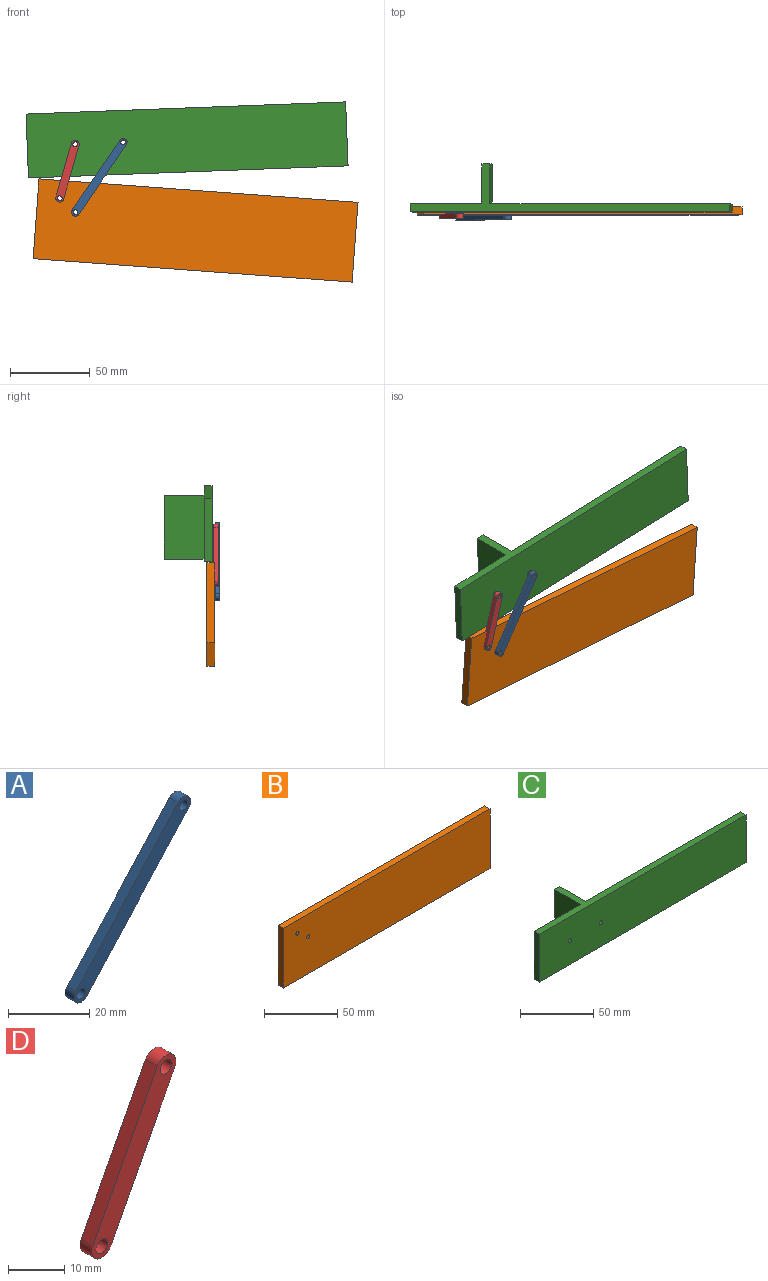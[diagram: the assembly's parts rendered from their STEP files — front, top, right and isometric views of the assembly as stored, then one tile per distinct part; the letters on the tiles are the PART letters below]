
ASSEMBLY  parts=4 mates=5
PART A: 8 faces, bbox 40.6x3x44 mm
  f0: plane 39.02x35.58mm, normal (-0.74,0,0.67), area 158.4mm2, adj f1,f3,f6,f7
  f1: cylinder r=2.5mm len=4.35mm, axis (0,1,0), area 23.6mm2, adj f0,f2,f6,f7
  f2: plane 39.02x35.58mm, normal (0.74,0,-0.67), area 158.4mm2, adj f1,f3,f6,f7
  f3: cylinder r=2.5mm len=4.35mm, axis (0,1,0), area 23.6mm2, adj f0,f2,f6,f7
  f4: cylinder r=1.5mm len=3mm, axis (0,1,0), area 28.3mm2, adj f6,f7
  f5: cylinder r=1.5mm len=3mm, axis (0,1,0), area 28.3mm2, adj f6,f7
  f6: plane 44.02x40.58mm, normal (0,-1,0), area 269.5mm2, adj f0,f1,f2,f3,f4,f5
  f7: plane 44.02x40.58mm, normal (0,1,0), area 269.5mm2, adj f0,f1,f2,f3,f4,f5
PART B: 8 faces, bbox 200x5x50 mm
  f0: plane 200x5mm, normal (0,0,1), area 1000mm2, adj f1,f3,f4,f5
  f1: plane 50x5mm, normal (-1,0,0), area 250mm2, adj f0,f2,f4,f5
  f2: plane 200x5mm, normal (0,0,-1), area 1000mm2, adj f1,f3,f4,f5
  f3: plane 50x5mm, normal (1,0,0), area 250mm2, adj f0,f2,f4,f5
  f4: plane 200x50mm, normal (0,-1,0), area 9985.9mm2, adj f0,f1,f2,f3,f6,f7
  f5: plane 200x50mm, normal (0,1,0), area 9985.9mm2, adj f0,f1,f2,f3,f6,f7
  f6: cylinder r=1.5mm len=5mm, axis (0,1,0), area 47.1mm2, adj f4,f5
  f7: cylinder r=1.5mm len=5mm, axis (0,1,0), area 47.1mm2, adj f4,f5
PART C: 12 faces, bbox 200x30x40 mm
  f0: plane 150x40mm, normal (0,1,0), area 5992.9mm2, adj f1,f3,f4,f8,f11
  f1: plane 200x30mm, normal (0,0,1), area 1125mm2, adj f0,f2,f4,f5,f6,f7,f8,f9
  f2: plane 40x5mm, normal (-1,0,0), area 200mm2, adj f1,f3,f5,f6
  f3: plane 200x30mm, normal (0,0,-1), area 1125mm2, adj f0,f2,f4,f5,f6,f7,f8,f9
  f4: plane 40x5mm, normal (1,0,0), area 200mm2, adj f0,f1,f3,f5
  f5: plane 200x40mm, normal (0,-1,0), area 7985.9mm2, adj f1,f2,f3,f4,f10,f11
  f6: plane 45x40mm, normal (0,1,0), area 1792.9mm2, adj f1,f2,f3,f7,f10
  f7: plane 40x25mm, normal (-1,0,0), area 1000mm2, adj f1,f3,f6,f9
  f8: plane 40x25mm, normal (1,0,0), area 1000mm2, adj f0,f1,f3,f9
  f9: plane 40x5mm, normal (0,1,0), area 200mm2, adj f1,f3,f7,f8
  f10: cylinder r=1.5mm len=5mm, axis (0,1,0), area 47.1mm2, adj f5,f6
  f11: cylinder r=1.5mm len=5mm, axis (0,1,0), area 47.1mm2, adj f0,f5
PART D: 8 faces, bbox 21.2x3x36.1 mm
  f0: cylinder r=2.5mm len=4.72mm, axis (0,1,0), area 23.6mm2, adj f1,f4,f6,f7
  f1: plane 31.11x16.21mm, normal (0.89,0,-0.46), area 105.2mm2, adj f0,f2,f6,f7
  f2: cylinder r=2.5mm len=4.72mm, axis (0,1,0), area 23.6mm2, adj f1,f4,f6,f7
  f3: cylinder r=1.5mm len=3mm, axis (0,1,0), area 28.3mm2, adj f6,f7
  f4: plane 31.11x16.21mm, normal (-0.89,0,0.46), area 105.2mm2, adj f0,f2,f6,f7
  f5: cylinder r=1.5mm len=3mm, axis (0,1,0), area 28.3mm2, adj f6,f7
  f6: plane 36.11x21.21mm, normal (0,-1,0), area 180.9mm2, adj f0,f1,f2,f3,f4,f5
  f7: plane 36.11x21.21mm, normal (0,1,0), area 180.9mm2, adj f0,f1,f2,f3,f4,f5
PLACE A rot(axis=(0,-1,0),8.2deg) t=(-49.85,55.12,-52.24)mm
PLACE B rot(axis=(0,1,0),4.2deg) t=(-45.93,55.32,-46.86)mm fixed
PLACE C rot(axis=(0,-1,0),2.2deg) t=(-52.54,57.1,-46.27)mm
PLACE D rot(axis=(0,-1,0),11.6deg) t=(-48.71,56.14,-50.85)mm
MATE cylindrical A.f1 <-> B.f7  axis (0,1,0) through (-23.05,48.62,-67.64)mm
MATE cylindrical D.f0 <-> B.f6  axis (0,1,0) through (-32.95,51.14,-58.87)mm
MATE parallel C.f5 <-> B.f4  axis (0,-1,0) through (45.87,52.1,-2.5)mm
MATE cylindrical D.f2 <-> C.f10  axis (0,1,0) through (-23.32,51.14,-25.14)mm
MATE cylindrical A.f3 <-> C.f11  axis (0,1,0) through (6.64,48.62,-23.97)mm
